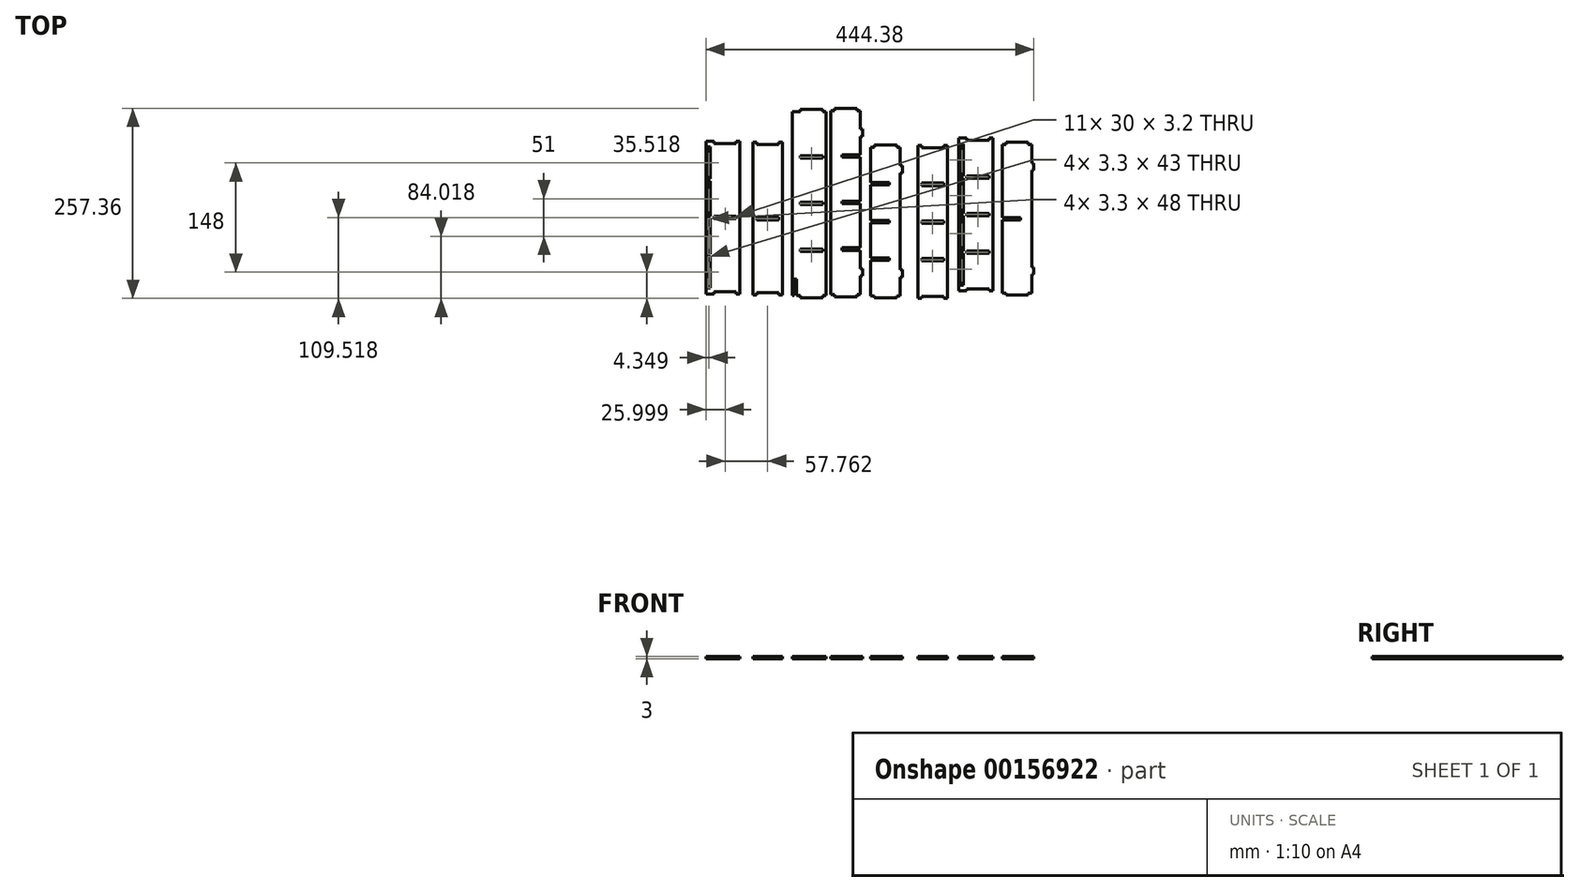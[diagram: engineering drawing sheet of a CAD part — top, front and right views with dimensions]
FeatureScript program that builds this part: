
annotation { "Feature Type Name" : "Feature", "Feature Type Description" : "" }
export const myFeature = defineFeature(function(context is Context, id is Id, definition is map)
    precondition{}
    {
        {
            var Q0;
            Q0=qCreatedBy(makeId("Top.planeOp"),FACE);
            var sketch = newSketch(context, id + "F0", { "sketchPlane" : qUnion([Q0])});
            skLineSegment(sketch, "E0.bottom", {"start": v(-73.2, 125.85) * mm, "end": v(-43.2, 125.85) * mm});
            skLineSegment(sketch, "E0.top", {"start": v(-73.2, -129.15) * mm, "end": v(-43.2, -129.15) * mm});
            skLineSegment(sketch, "E0.left", {"start": v(-78.2, 122.85) * mm, "end": v(-78.2, -126.15) * mm});
            skLineSegment(sketch, "E0.right", {"start": v(-38.2, 122.85) * mm, "end": v(-38.2, 97.85) * mm});
            skLineSegment(sketch, "E1", {"start": v(-38.2, 97.85) * mm, "end": v(-35.2, 97.85) * mm});
            skLineSegment(sketch, "E2", {"start": v(-35.2, 97.85) * mm, "end": v(-35.2, 87.85) * mm});
            skLineSegment(sketch, "E3", {"start": v(-35.2, 87.85) * mm, "end": v(-38.2, 87.85) * mm});
            skLineSegment(sketch, "E4", {"start": v(-38.2, -91.15) * mm, "end": v(-35.2, -91.15) * mm});
            skLineSegment(sketch, "E5", {"start": v(-35.2, -91.15) * mm, "end": v(-35.2, -101.15) * mm});
            skLineSegment(sketch, "E6", {"start": v(-35.2, -101.15) * mm, "end": v(-38.2, -101.15) * mm});
            skLineSegment(sketch, "E7", {"start": v(-78.2, 122.85) * mm, "end": v(-73.2, 122.85) * mm});
            skLineSegment(sketch, "E8", {"start": v(-73.2, 122.85) * mm, "end": v(-73.2, 125.85) * mm});
            skLineSegment(sketch, "E9", {"start": v(-43.2, 125.85) * mm, "end": v(-43.2, 122.85) * mm});
            skLineSegment(sketch, "E10", {"start": v(-43.2, 122.85) * mm, "end": v(-38.2, 122.85) * mm});
            skLineSegment(sketch, "E11", {"start": v(-78.2, -126.15) * mm, "end": v(-73.2, -126.15) * mm});
            skLineSegment(sketch, "E12", {"start": v(-73.2, -126.15) * mm, "end": v(-73.2, -129.15) * mm});
            skLineSegment(sketch, "E13", {"start": v(-43.2, -129.15) * mm, "end": v(-43.2, -126.15) * mm});
            skLineSegment(sketch, "E14", {"start": v(-43.2, -126.15) * mm, "end": v(-38.2, -126.15) * mm});
            skLineSegment(sketch, "E15.trimOffspring", {"start": v(-38.2, 87.85) * mm, "end": v(-38.2, 62.95) * mm});
            skLineSegment(sketch, "E16.trimOffspring", {"start": v(-38.2, -101.15) * mm, "end": v(-38.2, -126.15) * mm});
            skLineSegment(sketch, "E17", {"start": v(-38.2, 62.95) * mm, "end": v(-63.2, 62.95) * mm});
            skLineSegment(sketch, "E18", {"start": v(-63.2, 62.95) * mm, "end": v(-63.2, 59.75) * mm});
            skLineSegment(sketch, "E19", {"start": v(-63.2, 59.75) * mm, "end": v(-38.2, 59.75) * mm});
            skLineSegment(sketch, "E20.trimOffspring", {"start": v(-38.2, 59.75) * mm, "end": v(-38.2, -0.05) * mm});
            skLineSegment(sketch, "E21.0.1.0", {"start": v(-38.2, -0.05) * mm, "end": v(-63.2, -0.05) * mm});
            skLineSegment(sketch, "E21.0.1.1", {"start": v(-63.2, -3.25) * mm, "end": v(-38.2, -3.25) * mm});
            skLineSegment(sketch, "E21.0.1.2", {"start": v(-63.2, -0.05) * mm, "end": v(-63.2, -3.25) * mm});
            skLineSegment(sketch, "E21.0.2.0", {"start": v(-38.2, -63.05) * mm, "end": v(-63.2, -63.05) * mm});
            skLineSegment(sketch, "E21.0.2.1", {"start": v(-63.2, -66.25) * mm, "end": v(-38.2, -66.25) * mm});
            skLineSegment(sketch, "E21.0.2.2", {"start": v(-63.2, -63.05) * mm, "end": v(-63.2, -66.25) * mm});
            skLineSegment(sketch, "E21.direction1", {"start": v(-63.2, 59.75) * mm, "end": v(-38.2, 59.75) * mm, "construction": true});
            skLineSegment(sketch, "E22.trimOffspring", {"start": v(-38.2, -3.25) * mm, "end": v(-38.2, -63.05) * mm});
            skLineSegment(sketch, "E23.trimOffspring", {"start": v(-38.2, -66.25) * mm, "end": v(-38.2, -91.15) * mm});
            skSolve(sketch);
        }
        {
            var Q0;
            Q0=qSketchRegion(id+"F0",true);
            extrude(context, id + "F1", {"entities" : qUnion([Q0]), "depth" : 3 * mm});
        }
        {
            var Q0;
            Q0=qCreatedBy(makeId("Top.planeOp"),FACE);
            var sketch = newSketch(context, id + "F2", { "sketchPlane" : qUnion([Q0])});
            skLineSegment(sketch, "E24.bottom", {"start": v(-19.23, 76.16) * mm, "end": v(10.77, 76.16) * mm});
            skLineSegment(sketch, "E24.top", {"start": v(-19.23, -130.84) * mm, "end": v(10.77, -130.84) * mm});
            skLineSegment(sketch, "E24.left", {"start": v(-24.23, 73.16) * mm, "end": v(-24.23, 25.26) * mm});
            skLineSegment(sketch, "E24.right", {"start": v(15.77, 73.16) * mm, "end": v(15.77, 48.16) * mm});
            skLineSegment(sketch, "E25", {"start": v(-24.23, 73.16) * mm, "end": v(-19.23, 73.16) * mm});
            skLineSegment(sketch, "E26", {"start": v(-19.23, 73.16) * mm, "end": v(-19.23, 76.16) * mm});
            skLineSegment(sketch, "E27", {"start": v(10.77, 76.16) * mm, "end": v(10.77, 73.16) * mm});
            skLineSegment(sketch, "E28", {"start": v(10.77, 73.16) * mm, "end": v(15.77, 73.16) * mm});
            skLineSegment(sketch, "E29", {"start": v(-24.23, -127.84) * mm, "end": v(-19.23, -127.84) * mm});
            skLineSegment(sketch, "E30", {"start": v(-19.23, -127.84) * mm, "end": v(-19.23, -130.84) * mm});
            skLineSegment(sketch, "E31", {"start": v(10.77, -130.84) * mm, "end": v(10.77, -127.84) * mm});
            skLineSegment(sketch, "E32", {"start": v(10.77, -127.84) * mm, "end": v(15.77, -127.84) * mm});
            skLineSegment(sketch, "E33", {"start": v(15.77, -102.84) * mm, "end": v(18.77, -102.84) * mm});
            skLineSegment(sketch, "E34", {"start": v(18.77, -102.84) * mm, "end": v(18.77, -92.84) * mm});
            skLineSegment(sketch, "E35", {"start": v(18.77, -92.84) * mm, "end": v(15.77, -92.84) * mm});
            skLineSegment(sketch, "E36", {"start": v(15.77, 48.16) * mm, "end": v(18.77, 48.16) * mm});
            skLineSegment(sketch, "E37", {"start": v(18.77, 48.16) * mm, "end": v(18.77, 38.16) * mm});
            skLineSegment(sketch, "E38", {"start": v(18.77, 38.16) * mm, "end": v(15.77, 38.16) * mm});
            skLineSegment(sketch, "E39.trimOffspring", {"start": v(15.77, 38.16) * mm, "end": v(15.77, -92.84) * mm});
            skLineSegment(sketch, "E40.trimOffspring", {"start": v(15.77, -102.84) * mm, "end": v(15.77, -127.84) * mm});
            skLineSegment(sketch, "E41", {"start": v(-24.23, 25.26) * mm, "end": v(0.77, 25.26) * mm});
            skLineSegment(sketch, "E42", {"start": v(0.77, 25.26) * mm, "end": v(0.77, 22.06) * mm});
            skLineSegment(sketch, "E43", {"start": v(0.77, 22.06) * mm, "end": v(-24.23, 22.06) * mm});
            skLineSegment(sketch, "E44.trimOffspring", {"start": v(-24.23, 22.06) * mm, "end": v(-24.23, -25.74) * mm});
            skLineSegment(sketch, "E45.0.1.0", {"start": v(-24.23, -25.74) * mm, "end": v(0.77, -25.74) * mm});
            skLineSegment(sketch, "E45.0.1.1", {"start": v(0.77, -28.94) * mm, "end": v(-24.23, -28.94) * mm});
            skLineSegment(sketch, "E45.0.1.2", {"start": v(0.77, -25.74) * mm, "end": v(0.77, -28.94) * mm});
            skLineSegment(sketch, "E45.0.2.0", {"start": v(-24.23, -76.74) * mm, "end": v(0.77, -76.74) * mm});
            skLineSegment(sketch, "E45.0.2.1", {"start": v(0.77, -79.94) * mm, "end": v(-24.23, -79.94) * mm});
            skLineSegment(sketch, "E45.0.2.2", {"start": v(0.77, -76.74) * mm, "end": v(0.77, -79.94) * mm});
            skLineSegment(sketch, "E45.direction1", {"start": v(-24.23, 22.06) * mm, "end": v(0.77, 22.06) * mm, "construction": true});
            skLineSegment(sketch, "E45.direction2", {"start": v(-24.23, 22.06) * mm, "end": v(-24.23, -25.74) * mm, "construction": true});
            skLineSegment(sketch, "E46.trimOffspring", {"start": v(-24.23, -28.94) * mm, "end": v(-24.23, -76.74) * mm});
            skLineSegment(sketch, "E47.trimOffspring", {"start": v(-24.23, -79.94) * mm, "end": v(-24.23, -127.84) * mm});
            skSolve(sketch);
        }
        {
            var Q0;
            Q0=qSketchRegion(id+"F2",true);
            extrude(context, id + "F3", {"entities" : qUnion([Q0]), "depth" : 3 * mm});
        }
        {
            var Q0;
            Q0=qCreatedBy(makeId("Top.planeOp"),FACE);
            var sketch = newSketch(context, id + "F4", { "sketchPlane" : qUnion([Q0])});
            skLineSegment(sketch, "E48.bottom", {"start": v(39.63, 75.5) * mm, "end": v(44.63, 75.5) * mm});
            skLineSegment(sketch, "E48.top", {"start": v(39.63, -131.5) * mm, "end": v(44.63, -131.5) * mm});
            skLineSegment(sketch, "E48.left", {"start": v(39.63, 75.5) * mm, "end": v(39.63, -131.5) * mm});
            skLineSegment(sketch, "E48.right", {"start": v(79.63, 75.5) * mm, "end": v(79.63, -131.5) * mm});
            skLineSegment(sketch, "E49", {"start": v(44.63, 75.5) * mm, "end": v(44.63, 72.5) * mm});
            skLineSegment(sketch, "E50", {"start": v(44.63, 72.5) * mm, "end": v(74.63, 72.5) * mm});
            skLineSegment(sketch, "E51", {"start": v(74.63, 72.5) * mm, "end": v(74.63, 75.5) * mm});
            skLineSegment(sketch, "E52.trimOffspring", {"start": v(74.63, 75.5) * mm, "end": v(79.63, 75.5) * mm});
            skLineSegment(sketch, "E53.bottom", {"start": v(44.63, 24.6) * mm, "end": v(74.63, 24.6) * mm});
            skLineSegment(sketch, "E53.top", {"start": v(44.63, 21.4) * mm, "end": v(74.63, 21.4) * mm});
            skLineSegment(sketch, "E53.left", {"start": v(44.63, 24.6) * mm, "end": v(44.63, 21.4) * mm});
            skLineSegment(sketch, "E53.right", {"start": v(74.63, 24.6) * mm, "end": v(74.63, 21.4) * mm});
            skLineSegment(sketch, "E54.0.1.0", {"start": v(44.63, -26.4) * mm, "end": v(74.63, -26.4) * mm});
            skLineSegment(sketch, "E54.0.1.1", {"start": v(44.63, -29.6) * mm, "end": v(74.63, -29.6) * mm});
            skLineSegment(sketch, "E54.0.1.2", {"start": v(44.63, -26.4) * mm, "end": v(44.63, -29.6) * mm});
            skLineSegment(sketch, "E54.0.1.3", {"start": v(74.63, -26.4) * mm, "end": v(74.63, -29.6) * mm});
            skLineSegment(sketch, "E54.0.2.0", {"start": v(44.63, -77.4) * mm, "end": v(74.63, -77.4) * mm});
            skLineSegment(sketch, "E54.0.2.1", {"start": v(44.63, -80.6) * mm, "end": v(74.63, -80.6) * mm});
            skLineSegment(sketch, "E54.0.2.2", {"start": v(44.63, -77.4) * mm, "end": v(44.63, -80.6) * mm});
            skLineSegment(sketch, "E54.0.2.3", {"start": v(74.63, -77.4) * mm, "end": v(74.63, -80.6) * mm});
            skLineSegment(sketch, "E54.direction1", {"start": v(44.63, 21.4) * mm, "end": v(69.63, 21.4) * mm, "construction": true});
            skLineSegment(sketch, "E54.direction2", {"start": v(44.63, 21.4) * mm, "end": v(44.63, -29.6) * mm, "construction": true});
            skLineSegment(sketch, "E55", {"start": v(44.63, -131.5) * mm, "end": v(44.63, -128.5) * mm});
            skLineSegment(sketch, "E56", {"start": v(44.63, -128.5) * mm, "end": v(74.63, -128.5) * mm});
            skLineSegment(sketch, "E57", {"start": v(74.63, -128.5) * mm, "end": v(74.63, -131.5) * mm});
            skLineSegment(sketch, "E58.trimOffspring", {"start": v(74.63, -131.5) * mm, "end": v(79.63, -131.5) * mm});
            skSolve(sketch);
        }
        {
            var Q0;
            Q0=qSketchRegion(id+"F4",true);
            extrude(context, id + "F5", {"entities" : qUnion([Q0]), "depth" : 3 * mm});
        }
        {
            var Q0;
            Q0=qCreatedBy(makeId("Top.planeOp"),FACE);
            var sketch = newSketch(context, id + "F6", { "sketchPlane" : qUnion([Q0])});
            skLineSegment(sketch, "E59.bottom", {"start": v(94.98, 85.55) * mm, "end": v(105.98, 85.55) * mm});
            skLineSegment(sketch, "E59.top", {"start": v(94.98, -121.45) * mm, "end": v(105.98, -121.45) * mm});
            skLineSegment(sketch, "E59.left", {"start": v(94.98, 85.55) * mm, "end": v(94.98, -121.45) * mm});
            skLineSegment(sketch, "E59.right", {"start": v(140.98, 85.55) * mm, "end": v(140.98, -121.45) * mm});
            skLineSegment(sketch, "E60", {"start": v(105.98, 85.55) * mm, "end": v(105.98, 82.55) * mm});
            skLineSegment(sketch, "E61", {"start": v(105.98, 82.55) * mm, "end": v(135.98, 82.55) * mm});
            skLineSegment(sketch, "E62", {"start": v(135.98, 82.55) * mm, "end": v(135.98, 85.55) * mm});
            skLineSegment(sketch, "E63", {"start": v(105.98, -121.45) * mm, "end": v(105.98, -118.45) * mm});
            skLineSegment(sketch, "E64", {"start": v(105.98, -118.45) * mm, "end": v(135.98, -118.45) * mm});
            skLineSegment(sketch, "E65", {"start": v(135.98, -118.45) * mm, "end": v(135.98, -121.45) * mm});
            skLineSegment(sketch, "E66.trimOffspring", {"start": v(135.98, 85.55) * mm, "end": v(140.98, 85.55) * mm});
            skLineSegment(sketch, "E67.bottom", {"start": v(105.98, 34.65) * mm, "end": v(135.98, 34.65) * mm});
            skLineSegment(sketch, "E67.top", {"start": v(105.98, 31.45) * mm, "end": v(135.98, 31.45) * mm});
            skLineSegment(sketch, "E67.left", {"start": v(105.98, 34.65) * mm, "end": v(105.98, 31.45) * mm});
            skLineSegment(sketch, "E67.right", {"start": v(135.98, 34.65) * mm, "end": v(135.98, 31.45) * mm});
            skLineSegment(sketch, "E68.0.1.0", {"start": v(135.98, -16.35) * mm, "end": v(135.98, -19.55) * mm});
            skLineSegment(sketch, "E68.0.1.1", {"start": v(105.98, -16.35) * mm, "end": v(105.98, -19.55) * mm});
            skLineSegment(sketch, "E68.0.1.2", {"start": v(105.98, -16.35) * mm, "end": v(135.98, -16.35) * mm});
            skLineSegment(sketch, "E68.0.1.3", {"start": v(105.98, -19.55) * mm, "end": v(135.98, -19.55) * mm});
            skLineSegment(sketch, "E68.0.2.0", {"start": v(135.98, -67.35) * mm, "end": v(135.98, -70.55) * mm});
            skLineSegment(sketch, "E68.0.2.1", {"start": v(105.98, -67.35) * mm, "end": v(105.98, -70.55) * mm});
            skLineSegment(sketch, "E68.0.2.2", {"start": v(105.98, -67.35) * mm, "end": v(135.98, -67.35) * mm});
            skLineSegment(sketch, "E68.0.2.3", {"start": v(105.98, -70.55) * mm, "end": v(135.98, -70.55) * mm});
            skLineSegment(sketch, "E68.direction1", {"start": v(105.98, 31.45) * mm, "end": v(130.98, 31.45) * mm, "construction": true});
            skLineSegment(sketch, "E68.direction2", {"start": v(105.98, 31.45) * mm, "end": v(105.98, -19.55) * mm, "construction": true});
            skLineSegment(sketch, "E69.trimOffspring", {"start": v(135.98, -121.45) * mm, "end": v(140.98, -121.45) * mm});
            skLineSegment(sketch, "E70.bottom", {"start": v(97.68, 77.55) * mm, "end": v(100.98, 77.55) * mm});
            skLineSegment(sketch, "E70.top", {"start": v(97.68, 34.55) * mm, "end": v(100.98, 34.55) * mm});
            skLineSegment(sketch, "E70.left", {"start": v(97.68, 77.55) * mm, "end": v(97.68, 34.55) * mm});
            skLineSegment(sketch, "E70.right", {"start": v(100.98, 77.55) * mm, "end": v(100.98, 34.55) * mm});
            skLineSegment(sketch, "E71.bottom", {"start": v(100.98, 31.55) * mm, "end": v(97.68, 31.55) * mm});
            skLineSegment(sketch, "E71.top", {"start": v(100.98, -16.45) * mm, "end": v(97.68, -16.45) * mm});
            skLineSegment(sketch, "E71.left", {"start": v(100.98, 31.55) * mm, "end": v(100.98, -16.45) * mm});
            skLineSegment(sketch, "E71.right", {"start": v(97.68, 31.55) * mm, "end": v(97.68, -16.45) * mm});
            skLineSegment(sketch, "E72.bottom", {"start": v(100.98, -19.45) * mm, "end": v(97.68, -19.45) * mm});
            skLineSegment(sketch, "E72.top", {"start": v(100.98, -67.45) * mm, "end": v(97.68, -67.45) * mm});
            skLineSegment(sketch, "E72.left", {"start": v(100.98, -19.45) * mm, "end": v(100.98, -67.45) * mm});
            skLineSegment(sketch, "E72.right", {"start": v(97.68, -19.45) * mm, "end": v(97.68, -67.45) * mm});
            skLineSegment(sketch, "E73.bottom", {"start": v(100.98, -70.45) * mm, "end": v(97.68, -70.45) * mm});
            skLineSegment(sketch, "E73.top", {"start": v(100.98, -113.45) * mm, "end": v(97.68, -113.45) * mm});
            skLineSegment(sketch, "E73.left", {"start": v(100.98, -70.45) * mm, "end": v(100.98, -113.45) * mm});
            skLineSegment(sketch, "E73.right", {"start": v(97.68, -70.45) * mm, "end": v(97.68, -113.45) * mm});
            skSolve(sketch);
        }
        {
            var Q0;
            Q0=qSketchRegion(id+"F6",true);
            extrude(context, id + "F7", {"entities" : qUnion([Q0]), "depth" : 3 * mm});
        }
        {
            var Q0;
            Q0=qCreatedBy(makeId("Top.planeOp"),FACE);
            var sketch = newSketch(context, id + "F8", { "sketchPlane" : qUnion([Q0])});
            skLineSegment(sketch, "E74.bottom", {"start": v(-89.55, 124.5) * mm, "end": v(-119.55, 124.5) * mm});
            skLineSegment(sketch, "E74.top", {"start": v(-89.55, -130.5) * mm, "end": v(-119.55, -130.5) * mm});
            skLineSegment(sketch, "E74.left", {"start": v(-84.55, 121.5) * mm, "end": v(-84.55, -127.5) * mm});
            skLineSegment(sketch, "E74.right", {"start": v(-130.55, 121.5) * mm, "end": v(-130.55, -127.5) * mm});
            skLineSegment(sketch, "E75", {"start": v(-130.55, 121.5) * mm, "end": v(-119.55, 121.5) * mm});
            skLineSegment(sketch, "E76", {"start": v(-119.55, 121.5) * mm, "end": v(-119.55, 124.5) * mm});
            skLineSegment(sketch, "E77", {"start": v(-89.55, 124.5) * mm, "end": v(-89.55, 121.5) * mm});
            skLineSegment(sketch, "E78", {"start": v(-89.55, 121.5) * mm, "end": v(-84.55, 121.5) * mm});
            skLineSegment(sketch, "E79", {"start": v(-130.55, -127.5) * mm, "end": v(-127.85, -127.5) * mm});
            skLineSegment(sketch, "E80", {"start": v(-119.55, -127.5) * mm, "end": v(-119.55, -130.5) * mm});
            skLineSegment(sketch, "E81", {"start": v(-89.55, -130.5) * mm, "end": v(-89.55, -127.5) * mm});
            skLineSegment(sketch, "E82", {"start": v(-89.55, -127.5) * mm, "end": v(-84.55, -127.5) * mm});
            skLineSegment(sketch, "E83.bottom", {"start": v(-119.55, -67.6) * mm, "end": v(-89.55, -67.6) * mm});
            skLineSegment(sketch, "E83.top", {"start": v(-119.55, -64.4) * mm, "end": v(-89.55, -64.4) * mm});
            skLineSegment(sketch, "E83.left", {"start": v(-119.55, -67.6) * mm, "end": v(-119.55, -64.4) * mm});
            skLineSegment(sketch, "E83.right", {"start": v(-89.55, -67.6) * mm, "end": v(-89.55, -64.4) * mm});
            skLineSegment(sketch, "E84.0.1.0", {"start": v(-119.55, -4.6) * mm, "end": v(-89.55, -4.6) * mm});
            skLineSegment(sketch, "E84.0.1.1", {"start": v(-119.55, -1.4) * mm, "end": v(-89.55, -1.4) * mm});
            skLineSegment(sketch, "E84.0.1.2", {"start": v(-119.55, -4.6) * mm, "end": v(-119.55, -1.4) * mm});
            skLineSegment(sketch, "E84.0.1.3", {"start": v(-89.55, -4.6) * mm, "end": v(-89.55, -1.4) * mm});
            skLineSegment(sketch, "E84.0.2.0", {"start": v(-119.55, 58.4) * mm, "end": v(-89.55, 58.4) * mm});
            skLineSegment(sketch, "E84.0.2.1", {"start": v(-119.55, 61.6) * mm, "end": v(-89.55, 61.6) * mm});
            skLineSegment(sketch, "E84.0.2.2", {"start": v(-119.55, 58.4) * mm, "end": v(-119.55, 61.6) * mm});
            skLineSegment(sketch, "E84.0.2.3", {"start": v(-89.55, 58.4) * mm, "end": v(-89.55, 61.6) * mm});
            skLineSegment(sketch, "E84.direction1", {"start": v(-119.55, -67.6) * mm, "end": v(-94.55, -67.6) * mm, "construction": true});
            skLineSegment(sketch, "E84.direction2", {"start": v(-119.55, -67.6) * mm, "end": v(-119.55, -4.6) * mm, "construction": true});
            skLineSegment(sketch, "E85", {"start": v(-127.85, -127.5) * mm, "end": v(-127.85, -105.5) * mm});
            skLineSegment(sketch, "E86", {"start": v(-127.85, -105.5) * mm, "end": v(-124.55, -105.5) * mm});
            skLineSegment(sketch, "E87", {"start": v(-124.55, -105.5) * mm, "end": v(-124.55, -127.5) * mm});
            skLineSegment(sketch, "E88.trimOffspring", {"start": v(-124.55, -127.5) * mm, "end": v(-119.55, -127.5) * mm});
            skSolve(sketch);
        }
        {
            var Q0;
            Q0=qSketchRegion(id+"F8",true);
            extrude(context, id + "F9", {"entities" : qUnion([Q0]), "depth" : 3 * mm});
        }
        {
            var Q0;
            Q0=qCreatedBy(makeId("Top.planeOp"),FACE);
            var sketch = newSketch(context, id + "F10", { "sketchPlane" : qUnion([Q0])});
            skLineSegment(sketch, "E89.bottom", {"start": v(158.73, 79.86) * mm, "end": v(188.73, 79.86) * mm});
            skLineSegment(sketch, "E89.top", {"start": v(158.73, -127.14) * mm, "end": v(188.73, -127.14) * mm});
            skLineSegment(sketch, "E89.right", {"start": v(193.73, 76.86) * mm, "end": v(193.73, 51.86) * mm});
            skLineSegment(sketch, "E90", {"start": v(153.73, 76.86) * mm, "end": v(158.73, 76.86) * mm});
            skLineSegment(sketch, "E91", {"start": v(158.73, 76.86) * mm, "end": v(158.73, 79.86) * mm});
            skLineSegment(sketch, "E92", {"start": v(188.73, 79.86) * mm, "end": v(188.73, 76.86) * mm});
            skLineSegment(sketch, "E93", {"start": v(188.73, 76.86) * mm, "end": v(193.73, 76.86) * mm});
            skLineSegment(sketch, "E94", {"start": v(153.73, -124.14) * mm, "end": v(158.73, -124.14) * mm});
            skLineSegment(sketch, "E95", {"start": v(158.73, -124.14) * mm, "end": v(158.73, -127.14) * mm});
            skLineSegment(sketch, "E96", {"start": v(188.73, -127.14) * mm, "end": v(188.73, -124.14) * mm});
            skLineSegment(sketch, "E97", {"start": v(188.73, -124.14) * mm, "end": v(193.73, -124.14) * mm});
            skLineSegment(sketch, "E98", {"start": v(193.73, -99.14) * mm, "end": v(196.73, -99.14) * mm});
            skLineSegment(sketch, "E99", {"start": v(196.73, -99.14) * mm, "end": v(196.73, -89.14) * mm});
            skLineSegment(sketch, "E100", {"start": v(196.73, -89.14) * mm, "end": v(193.73, -89.14) * mm});
            skLineSegment(sketch, "E101", {"start": v(193.73, 51.86) * mm, "end": v(196.73, 51.86) * mm});
            skLineSegment(sketch, "E102", {"start": v(196.73, 51.86) * mm, "end": v(196.73, 41.86) * mm});
            skLineSegment(sketch, "E103", {"start": v(196.73, 41.86) * mm, "end": v(193.73, 41.86) * mm});
            skLineSegment(sketch, "E104.trimOffspring", {"start": v(193.73, 41.86) * mm, "end": v(193.73, -89.14) * mm});
            skLineSegment(sketch, "E105.trimOffspring", {"start": v(193.73, -99.14) * mm, "end": v(193.73, -124.14) * mm});
            skLineSegment(sketch, "E106.0.1.0", {"start": v(153.73, -22.04) * mm, "end": v(178.73, -22.04) * mm});
            skLineSegment(sketch, "E106.0.1.1", {"start": v(178.73, -25.24) * mm, "end": v(153.73, -25.24) * mm});
            skLineSegment(sketch, "E106.0.1.2", {"start": v(178.73, -22.04) * mm, "end": v(178.73, -25.24) * mm});
            skLineSegment(sketch, "E107", {"start": v(153.73, 76.86) * mm, "end": v(153.73, -22.04) * mm});
            skLineSegment(sketch, "E108", {"start": v(153.73, -25.24) * mm, "end": v(153.73, -124.14) * mm});
            skSolve(sketch);
        }
        {
            var Q0;
            Q0=qSketchRegion(id+"F10",true);
            extrude(context, id + "F11", {"entities" : qUnion([Q0]), "depth" : 3 * mm});
        }
        {
            var Q0;
            Q0=qCreatedBy(makeId("Top.planeOp"),FACE);
            var sketch = newSketch(context, id + "F12", { "sketchPlane" : qUnion([Q0])});
            skLineSegment(sketch, "E109.bottom", {"start": v(-183.89, 80.14) * mm, "end": v(-178.89, 80.14) * mm});
            skLineSegment(sketch, "E109.top", {"start": v(-183.89, -126.86) * mm, "end": v(-178.89, -126.86) * mm});
            skLineSegment(sketch, "E109.left", {"start": v(-183.89, 80.14) * mm, "end": v(-183.89, -126.86) * mm});
            skLineSegment(sketch, "E109.right", {"start": v(-143.89, 80.14) * mm, "end": v(-143.89, -126.86) * mm});
            skLineSegment(sketch, "E110", {"start": v(-178.89, 80.14) * mm, "end": v(-178.89, 77.14) * mm});
            skLineSegment(sketch, "E111", {"start": v(-178.89, 77.14) * mm, "end": v(-148.89, 77.14) * mm});
            skLineSegment(sketch, "E112", {"start": v(-148.89, 77.14) * mm, "end": v(-148.89, 80.14) * mm});
            skLineSegment(sketch, "E113.trimOffspring", {"start": v(-148.89, 80.14) * mm, "end": v(-143.89, 80.14) * mm});
            skLineSegment(sketch, "E114.0.1.0", {"start": v(-178.89, -21.76) * mm, "end": v(-148.89, -21.76) * mm});
            skLineSegment(sketch, "E114.0.1.1", {"start": v(-178.89, -24.96) * mm, "end": v(-148.89, -24.96) * mm});
            skLineSegment(sketch, "E114.0.1.2", {"start": v(-178.89, -21.76) * mm, "end": v(-178.89, -24.96) * mm});
            skLineSegment(sketch, "E114.0.1.3", {"start": v(-148.89, -21.76) * mm, "end": v(-148.89, -24.96) * mm});
            skLineSegment(sketch, "E114.direction2", {"start": v(-178.89, -21.76) * mm, "end": v(-178.89, -24.96) * mm, "construction": true});
            skLineSegment(sketch, "E115", {"start": v(-178.89, -126.86) * mm, "end": v(-178.89, -123.86) * mm});
            skLineSegment(sketch, "E116", {"start": v(-178.89, -123.86) * mm, "end": v(-148.89, -123.86) * mm});
            skLineSegment(sketch, "E117", {"start": v(-148.89, -123.86) * mm, "end": v(-148.89, -126.86) * mm});
            skLineSegment(sketch, "E118.trimOffspring", {"start": v(-148.89, -126.86) * mm, "end": v(-143.89, -126.86) * mm});
            skSolve(sketch);
        }
        {
            var Q0;
            Q0=qSketchRegion(id+"F12",true);
            extrude(context, id + "F13", {"entities" : qUnion([Q0]), "depth" : 3 * mm});
        }
        {
            var Q0;
            Q0=qCreatedBy(makeId("Top.planeOp"),FACE);
            var sketch = newSketch(context, id + "F14", { "sketchPlane" : qUnion([Q0])});
            skLineSegment(sketch, "E119.bottom", {"start": v(-247.65, 81.5) * mm, "end": v(-236.65, 81.5) * mm});
            skLineSegment(sketch, "E119.top", {"start": v(-247.65, -125.5) * mm, "end": v(-236.65, -125.5) * mm});
            skLineSegment(sketch, "E119.left", {"start": v(-247.65, 81.5) * mm, "end": v(-247.65, -125.5) * mm});
            skLineSegment(sketch, "E119.right", {"start": v(-201.65, 81.5) * mm, "end": v(-201.65, -125.5) * mm});
            skLineSegment(sketch, "E120", {"start": v(-236.65, 81.5) * mm, "end": v(-236.65, 78.5) * mm});
            skLineSegment(sketch, "E121", {"start": v(-236.65, 78.5) * mm, "end": v(-206.65, 78.5) * mm});
            skLineSegment(sketch, "E122", {"start": v(-206.65, 78.5) * mm, "end": v(-206.65, 81.5) * mm});
            skLineSegment(sketch, "E123", {"start": v(-236.65, -125.5) * mm, "end": v(-236.65, -122.5) * mm});
            skLineSegment(sketch, "E124", {"start": v(-236.65, -122.5) * mm, "end": v(-206.65, -122.5) * mm});
            skLineSegment(sketch, "E125", {"start": v(-206.65, -122.5) * mm, "end": v(-206.65, -125.5) * mm});
            skLineSegment(sketch, "E126.trimOffspring", {"start": v(-206.65, 81.5) * mm, "end": v(-201.65, 81.5) * mm});
            skLineSegment(sketch, "E127.0.1.0", {"start": v(-206.65, -20.4) * mm, "end": v(-206.65, -23.6) * mm});
            skLineSegment(sketch, "E127.0.1.1", {"start": v(-236.65, -20.4) * mm, "end": v(-236.65, -23.6) * mm});
            skLineSegment(sketch, "E127.0.1.2", {"start": v(-236.65, -20.4) * mm, "end": v(-206.65, -20.4) * mm});
            skLineSegment(sketch, "E127.0.1.3", {"start": v(-236.65, -23.6) * mm, "end": v(-206.65, -23.6) * mm});
            skLineSegment(sketch, "E127.direction2", {"start": v(-236.65, -20.4) * mm, "end": v(-236.65, -23.6) * mm, "construction": true});
            skLineSegment(sketch, "E128.trimOffspring", {"start": v(-206.65, -125.5) * mm, "end": v(-201.65, -125.5) * mm});
            skLineSegment(sketch, "E129.bottom", {"start": v(-244.95, 73.5) * mm, "end": v(-241.65, 73.5) * mm});
            skLineSegment(sketch, "E129.top", {"start": v(-244.95, 30.5) * mm, "end": v(-241.65, 30.5) * mm});
            skLineSegment(sketch, "E129.left", {"start": v(-244.95, 73.5) * mm, "end": v(-244.95, 30.5) * mm});
            skLineSegment(sketch, "E129.right", {"start": v(-241.65, 73.5) * mm, "end": v(-241.65, 30.5) * mm});
            skLineSegment(sketch, "E130.bottom", {"start": v(-241.65, 27.5) * mm, "end": v(-244.95, 27.5) * mm});
            skLineSegment(sketch, "E130.top", {"start": v(-241.65, -20.5) * mm, "end": v(-244.95, -20.5) * mm});
            skLineSegment(sketch, "E130.left", {"start": v(-241.65, 27.5) * mm, "end": v(-241.65, -20.5) * mm});
            skLineSegment(sketch, "E130.right", {"start": v(-244.95, 27.5) * mm, "end": v(-244.95, -20.5) * mm});
            skLineSegment(sketch, "E131.bottom", {"start": v(-241.65, -23.5) * mm, "end": v(-244.95, -23.5) * mm});
            skLineSegment(sketch, "E131.top", {"start": v(-241.65, -71.5) * mm, "end": v(-244.95, -71.5) * mm});
            skLineSegment(sketch, "E131.left", {"start": v(-241.65, -23.5) * mm, "end": v(-241.65, -71.5) * mm});
            skLineSegment(sketch, "E131.right", {"start": v(-244.95, -23.5) * mm, "end": v(-244.95, -71.5) * mm});
            skLineSegment(sketch, "E132.bottom", {"start": v(-241.65, -74.5) * mm, "end": v(-244.95, -74.5) * mm});
            skLineSegment(sketch, "E132.top", {"start": v(-241.65, -117.5) * mm, "end": v(-244.95, -117.5) * mm});
            skLineSegment(sketch, "E132.left", {"start": v(-241.65, -74.5) * mm, "end": v(-241.65, -117.5) * mm});
            skLineSegment(sketch, "E132.right", {"start": v(-244.95, -74.5) * mm, "end": v(-244.95, -117.5) * mm});
            skSolve(sketch);
        }
        {
            var Q0;
            Q0=qSketchRegion(id+"F14",true);
            extrude(context, id + "F15", {"entities" : qUnion([Q0]), "depth" : 3 * mm});
        }
    });
